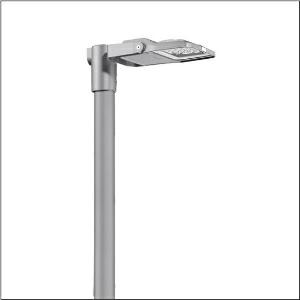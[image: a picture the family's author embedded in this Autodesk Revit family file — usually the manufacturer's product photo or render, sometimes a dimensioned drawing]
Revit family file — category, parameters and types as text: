
# Revit family: floodlight_fl_21_iq_micro___pl52_5xa7761a4d3a_5d98
name_source: partatom
category: Lighting Fixtures
units: mm (PartAtom-declared; Revit-internal decimal feet)

## family parameters
Cut with Voids When Loaded = No
Host = Face
Light Source = No
Part Type = Normal
Room Calculation Point = No
Round Connector Dimension = Use Diameter
Shared = No

## types (1)
- --- (1 x LED, 3010 lm, 23.1 W, 4000K)
    Apparent Load = 23 VA
    CIE Flux Codes = 26 60 98 100 100
    Color Rendering = 70
    Color Temperature = 4000K
    Default Elevation = 1800 mm
    Description = Floodlight FL 21 iQ micro, floodlight, primary light control with lens, of PMMA, primary optical cover: protective disc, of toughened safety glass, transparent, light distribution: PL52, light emission: direct distribution, installation type: surface-mounted, LED, High Power LED, rated luminous flux: 3.010lm, luminous efficacy: 130lm/W, light colour: 740, colour temperature: 4000K, control: optimised constant luminous flux control (CLO 2.0), Desk-Remote (wireless, voltage-free reading and setting of iQ features in the workshop via application-optimized NFC function/RFID function), Light-Fading, Smart-Wire, Night-Set, Lumen-Switch, Temp-Guard, Auto-Match, with terminal, 6-pole, mains connection: 220..240V, AC, 50/60Hz, start of lifetime: 23W, end of service life: 24W, reduction: 11W, luminaire housing, of diecast aluminium, powder-coated, Siteco® metallic grey (DB 702S), corrosivity category C5 mid according to DIN EN ISO 12944, sealing non-destructively replaceable, please order mast flange separately, mast bracket, of steel, galvanised, powder-coated, Siteco® metallic grey (DB 702S), protection rating (complete): IP66, insulation class (complete): insulation class II (safety insulation), certification: CE, ENEC, VDE, protection symbol: D, impact resistance: IK07, permissible operating ambient temperature: -40..+40°C, permissible operating ambient temperature for outdoor applications: -40..+50°C, standard: DIN EN 12944, LABS conformity tested according to VDMA 24364:2018-05, packaging unit: 1 piece

Light Distribution: PL52
    Height = 65 mm
    Lamp = 1 x LED
    Lamp Light Flux = 3010 lm
    Lamp Power = 23.1 W
    Lamp count = 1
    Length = 312 mm
    Luminous efficacy = 130 lm/W
    Manufacturer = Siteco
    ModVariant = No
    Model = 5XA7761A4D3A
    Number of Poles = 1
    OnlyDefault = Yes
    Power Factor = 1
    Product Name = Floodlight FL 21 iQ micro | PL52
    Product group = floodlight | pylon annexe
    ProductGroupID = 6200
    Protection Class = Protection class II
    Protection Degree = IP 66
    RLX_Detail_Level = 1
    RLX_Emergency_Light_Flux = 0 lm
    RLX_Emergency_Type = 0
    RLX_Emergency_Type_DB = No
    RlxData = <blob elided: 101901 chars, md5=aab6702f>
    Socket = socket
    Standby Power = 0 W
    System Light Flux = 3010 lm
    System Power = 23 W
    Type Comments = factory setting: luminous flux: 100 % | dim-lin: 254 | 455 mA
    Type Image = l_1007121.jpg
    URL = http://relux.com
    VarID = @adj_129175
    Voltage = 0 V
    Weight = 0.00 kg
    Width = 230 mm

## geometry (parser evidence)
native form markers: Blend x4, Sweep x12
no freeform markers — native parametric forms only
